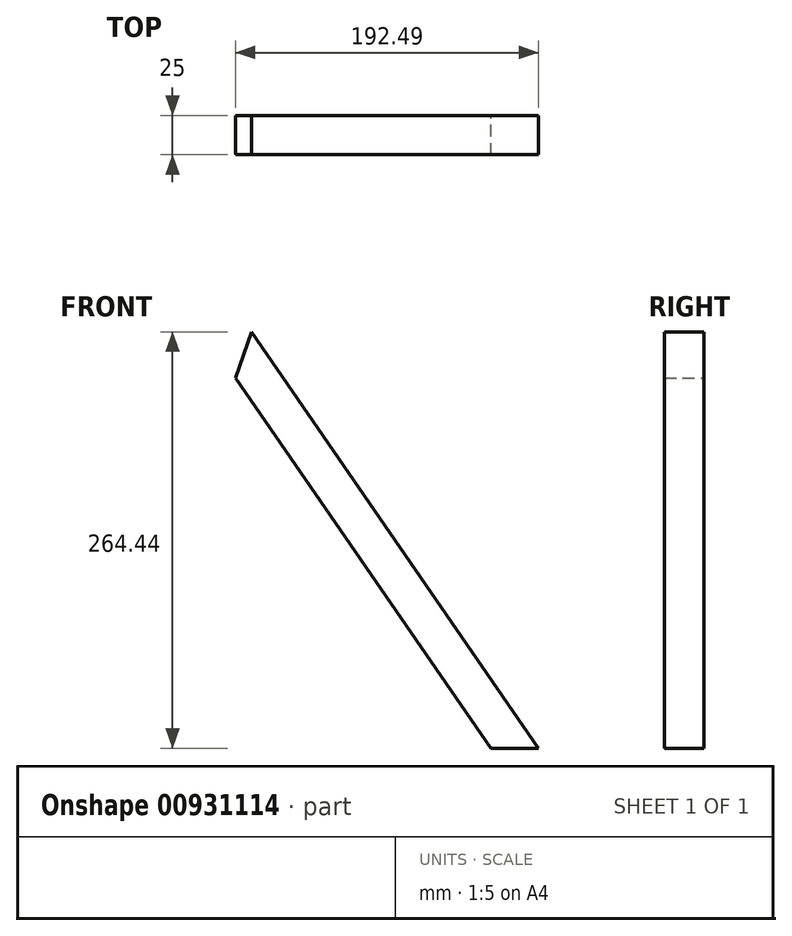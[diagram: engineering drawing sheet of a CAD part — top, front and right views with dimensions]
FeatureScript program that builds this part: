
annotation { "Feature Type Name" : "Feature", "Feature Type Description" : "" }
export const myFeature = defineFeature(function(context is Context, id is Id, definition is map)
    precondition{}
    {
        {
            var Q0;
            Q0=qCreatedBy(makeId("Front.planeOp"),FACE);
            var sketch = newSketch(context, id + "F0", { "sketchPlane" : qUnion([Q0])});
            skLineSegment(sketch, "E0", {"start": v(0, 0) * mm, "end": v(0, 580) * mm, "construction": true});
            skLineSegment(sketch, "E1", {"start": v(0, 580) * mm, "end": v(150, 580) * mm, "construction": true});
            skLineSegment(sketch, "E2.MirrorCS", {"start": v(0, 580) * mm, "end": v(-150, 580) * mm, "construction": true});
            skLineSegment(sketch, "E3", {"start": v(0, 0) * mm, "end": v(150, 0) * mm});
            skLineSegment(sketch, "E4.MirrorCS", {"start": v(0, 0) * mm, "end": v(-150, 0) * mm, "construction": true});
            skLineSegment(sketch, "E5", {"start": v(150, 580) * mm, "end": v(50, 580) * mm, "construction": true});
            skLineSegment(sketch, "E6", {"start": v(50, 580) * mm, "end": v(-150, 0) * mm, "construction": true});
            skLineSegment(sketch, "E7", {"start": v(-32.37, 264.44) * mm, "end": v(150, 0) * mm});
            skLineSegment(sketch, "E8", {"start": v(-42.5, 235.08) * mm, "end": v(119.63, 0) * mm});
            skLineSegment(sketch, "E9", {"start": v(119.63, 0) * mm, "end": v(150, 0) * mm, "construction": true});
            skLineSegment(sketch, "E10", {"start": v(-123.56, 0) * mm, "end": v(76.44, 580) * mm});
            skPoint(sketch, "E11.orphan", {"position": v(-50, 290) * mm});
            skLineSegment(sketch, "E12", {"start": v(-150, 0) * mm, "end": v(-126.37, -8.15) * mm, "construction": true});
            skLineSegment(sketch, "E13", {"start": v(-123.56, 0) * mm, "end": v(-126.37, -8.15) * mm, "construction": true});
            skLineSegment(sketch, "E14", {"start": v(41.38, 555) * mm, "end": v(-142.48, 555) * mm, "construction": true});
            skLineSegment(sketch, "E15", {"start": v(-150, 580) * mm, "end": v(-50, 580) * mm, "construction": true});
            skSolve(sketch);
        }
        {
            var Q0;
            Q0 = qSketchRegion(id + "F0", true);
            extrude(context, id + "F1", {"entities" : qUnion([Q0]), "depth" : 25 * mm, "offsetDistance" : 25 * mm});
        }
        {
            var Q0;
            Q0=makeQuery(id+"F1.opExtrude","SWEPT_FACE",FACE,{"disambiguationData":[OSD([sQuery(id+"F0.wireOp",EDGE,"E7")])]});
            cPlane(context, id + "F2", {"entities" : qUnion([Q0]), "cplaneType" : CPlaneType.OFFSET, "offset" : 0 * mm, "width" : 150 * mm, "height" : 150 * mm});
        }
    });
